# Revit family: Gira_217600
name_source: partatom
category: Elektroinstallationen
revit_build: Autodesk Revit 2017 (Build: 20160225_1515(x64)
units: mm (PartAtom-declared; Revit-internal decimal feet)

## family parameters
Basisbauteil = Fläche
Beim Laden mit Abzugskörper schneiden = Nein
Bemaßung runder Anschluss = Durchmesser verwenden
Beschriftungsausrichtung beibehalten = Nein
Gemeinsam genutzt = Nein
Raumberechnungspunkt = Nein
Teiletyp = Normal

## types (1)
- Gira_217600
    Andere Bussysteme = ohne
    BIM = https://media.stage.bim.site
    Beschreibung = KNX Stellantrieb 3   Merkmale:  Elektromotorischer Stellantrieb mit einem Binareingang (potenzialfrei) zur Montage auf ThermostatVentilunterteile (Empfehlung: Heimeier) zur Regelung von Heizungs oder Kühlsystemen.  Geeignet fur die Raumtemperaturregelung z. B. an Heizkörpern, Radiatoren, Konvektoren oder Heizkreisverteilern an Fusbodenheizungen usw.  Aufschrauben auf Ventilkopf.  Anschluss M30×1,5 mm.  Integrierter Busankoppler. Der Stellantrieb ist ein Proportionalantrieb und kann direkt (ohne zusätzlichen Busankoppler) in das KNX System integriert werden.  Versorgungsspannung wird aus dem KNX System bezogen.  Integrierter Temperatursensor.  Integrierter Raumtemperaturregler.  Mechanische Anzeige des Ventilhubs.  Automatische Erkennung des Ventilhubs.  Ein Eingang. Dieser ist nutzbar als Binäreingang oder zum Anschluss eines externen Temperatursensors mit den Funktionen:   Schalten, Dimmen, Jalousie, als Dimmwertgeber, als Temperaturwertgeber, als Helligkeitswertgeber, als Lichtszenennebenstelle mit und ohne Speicherfunktion, als Temperaturfernfühler oder als Temperaturbegrenzer für Fußbodenheizung.  Funktion Schalten: zwei unabhängige Schaltobjekte für jeden Eingang vorhanden (Schaltbefehle sind einzeln parametrierbar), Befehl bei steigender und fallender Flanke unabhängig einstellbar (EIN, AUS, UM, keine Reaktion).  Funktion Dimmen: Einflächen und Zweiflächenbedienung, Zeit zwischen Dimmen und Schalten, Telegrammwiederholung und Stopptelegramm senden möglich.  Funktion Jalousie: Befehl bei steigender Flanke einstellbar (keine Funktion, AUF, AB, UM), Bedienkonzept parametrierbar (Step  Move  Step oder Move  Step), Zeit zwischen Kurz und Langzeitbetrieb einstellbar (nur bei Step  Move  Step), Lamellenverstellzeit einstellbar.   Funktion Wertgeber: Flanke (Taster als Schließer, Taster als Öffner, Schalter) und Wert bei Flanke parametrierbar, Wertverstellung bei Taster über langen Tastendruck für Wertgeber möglich.  Lichtszenennebenstelle mit oder ohne Speicherfunktion.  Einsatz im Heizkreisverteiler möglich.  Schutz gegen festsitzende Ventile  Stellgröße (1 Bit oder 1 Byte).  Zyklische Überwachung der Stellgröße.  Störmeldeobjekt bei Antriebsfehler.  Notbetrieb über internen Temperatursensor.  2 Zwangsstellungen oder 1 Zwangsstellung und 1 Grenzwertobjekt einstellbar.  Minimale und maximale Stellgrößenbegrenzung einstellbar.  Hinweise :  In der Grundeinstellung passt der Stellantrieb auf Ventilunterteile der Fa. Heimeier. Für Ventilunterteile anderer Hersteller Adapter verwenden.
    Bussystem Funkbus = Nein
    Bussystem KNX = Ja
    Bussystem KNX-Funk = Nein
    Bussystem LON = Nein
    Bussystem Powernet = Nein
    Datenblatt = https://katalog.gira.de
    Funk bidirektional = Nein
    GTIN = 4010337019374
    HAN = 217600
    Hersteller = Gira
    Mit Busankopplung = Nein
    Montageart = Heizkörperventil
    Produktseite = http://katalog.gira.de
    Schutzart (IP) = IP20
    Typname = Stellantrieb 3 KNX
    URL = https://www.gira.de
    Vorgabe-Ansicht = 1219 mm

## geometry (parser evidence)
native form markers: Sweep x3
no freeform markers — native parametric forms only
